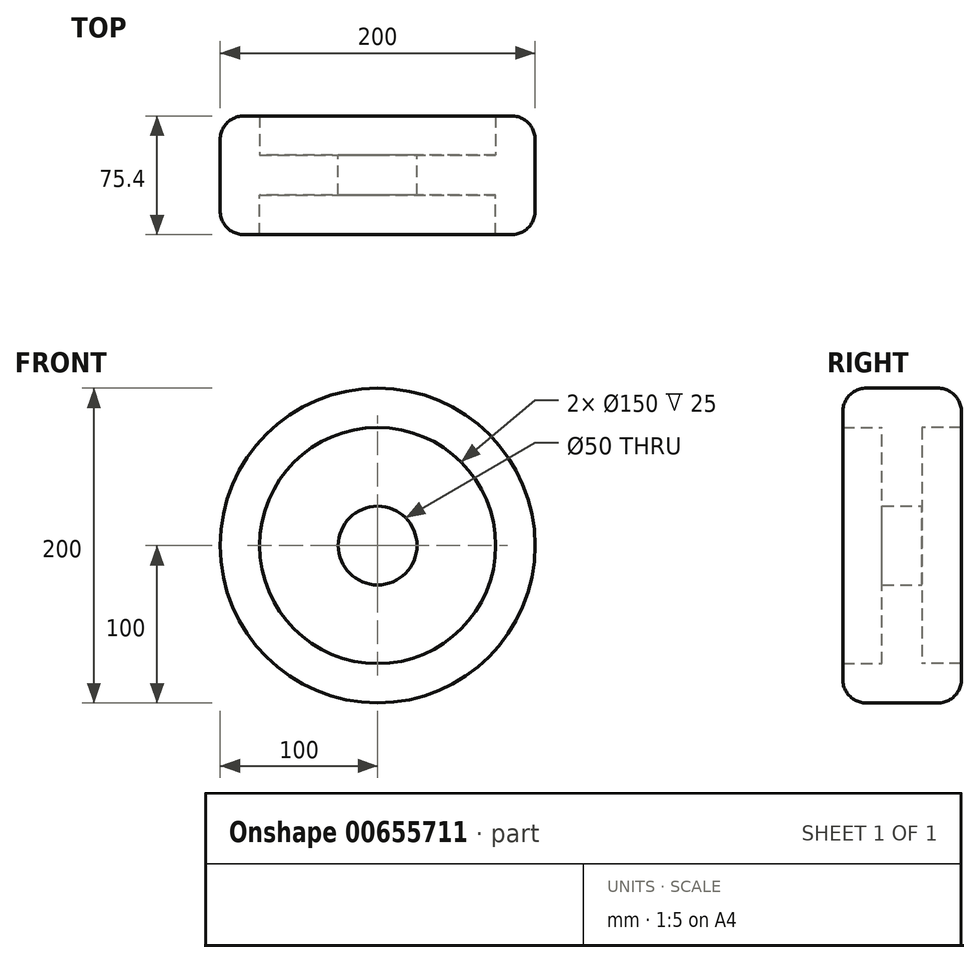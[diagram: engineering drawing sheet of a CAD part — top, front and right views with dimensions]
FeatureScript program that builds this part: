
annotation { "Feature Type Name" : "Feature", "Feature Type Description" : "" }
export const myFeature = defineFeature(function(context is Context, id is Id, definition is map)
    precondition{}
    {
        {
            var Q0;
            Q0=qCreatedBy(makeId("Front.planeOp"),FACE);
            var sketch = newSketch(context, id + "F0", { "sketchPlane" : qUnion([Q0])});
            skCircle(sketch, "E0", {"center": v(0, 0) * mm, "radius": 100 * mm});
            skCircle(sketch, "E1", {"center": v(0, 0) * mm, "radius": 75 * mm});
            skCircle(sketch, "E2", {"center": v(0, 0) * mm, "radius": 25 * mm});
            skSolve(sketch);
        }
        {
            var Q0;
            Q0=makeQuery(id+"F0.imprint","IMPRINT",FACE,{"disambiguationData":[TD([[makeQuery(id+"F0.imprint","IMPRINT",EDGE,{"derivedFrom":sQuery(id+"F0.wireOp",EDGE,"E0")}),1.0]])]});
            var Q1;
            Q1=makeQuery(id+"F0.imprint","IMPRINT",FACE,{"disambiguationData":[TD([[makeQuery(id+"F0.imprint","IMPRINT",EDGE,{"derivedFrom":sQuery(id+"F0.wireOp",EDGE,"E1")}),1.0]])]});
            extrude(context, id + "F1", {"entities" : qUnion([Q0, Q1]), "endBound" : BoundingType.SYMMETRIC, "depth" : 25.4 * mm, "offsetDistance" : 25.4 * mm});
        }
        {
            var Q0;
            Q0=makeQuery(id+"F1.opExtrude","CAP_FACE",FACE,{"disambiguationData":[OSD([sQuery(id+"F0.wireOp",EDGE,"E0"),sQuery(id+"F0.wireOp",EDGE,"E2")])],"isStart":false});
            var sketch = newSketch(context, id + "F2", { "sketchPlane" : qUnion([Q0])});
            skCircle(sketch, "E3", {"center": v(0, 0) * mm, "radius": 75 * mm});
            skSolve(sketch);
        }
        {
            var Q0;
            Q0=makeQuery(id+"F2.imprint","IMPRINT",FACE,{"disambiguationData":[TD([[makeQuery(id+"F2.imprint","IMPRINT",EDGE,{"derivedFrom":sQuery(id+"F2.wireOp",EDGE,"E3")}),-1.0]])]});
            extrude(context, id + "F3", {"entities" : qUnion([Q0]), "operationType" : NewBodyOperationType.ADD, "depth" : 25 * mm, "offsetDistance" : 25.4 * mm});
        }
        {
            var Q0;
            Q0=makeQuery(id+"F1.opExtrude","CAP_FACE",FACE,{"disambiguationData":[OSD([sQuery(id+"F0.wireOp",EDGE,"E0"),sQuery(id+"F0.wireOp",EDGE,"E2")])],"isStart":true});
            var sketch = newSketch(context, id + "F4", { "sketchPlane" : qUnion([Q0])});
            skCircle(sketch, "E4", {"center": v(0, 0) * mm, "radius": 75 * mm});
            skSolve(sketch);
        }
        {
            var Q0;
            Q0=makeQuery(id+"F4.imprint","IMPRINT",FACE,{"disambiguationData":[TD([[makeQuery(id+"F4.imprint","IMPRINT",EDGE,{"derivedFrom":sQuery(id+"F4.wireOp",EDGE,"E4")}),-1.0]])]});
            extrude(context, id + "F5", {"entities" : qUnion([Q0]), "operationType" : NewBodyOperationType.ADD, "depth" : 25 * mm, "offsetDistance" : 25.4 * mm});
        }
        {
            var Q0;
            Q0=makeQuery(id+"F5.opExtrude","CAP_EDGE",EDGE,{"disambiguationData":[OSD([sQuery(id+"F0.wireOp",EDGE,"E0")])],"isStart":false});
            var Q1;
            Q1=makeQuery(id+"F3.opExtrude","CAP_EDGE",EDGE,{"disambiguationData":[OSD([sQuery(id+"F0.wireOp",EDGE,"E0")])],"isStart":false});
            fillet(context, id + "F6", {"entities" : qUnion([Q0, Q1]), "radius" : 15 * mm, "tangentPropagation" : true, "allowEdgeOverflow" : false});
        }
    });
